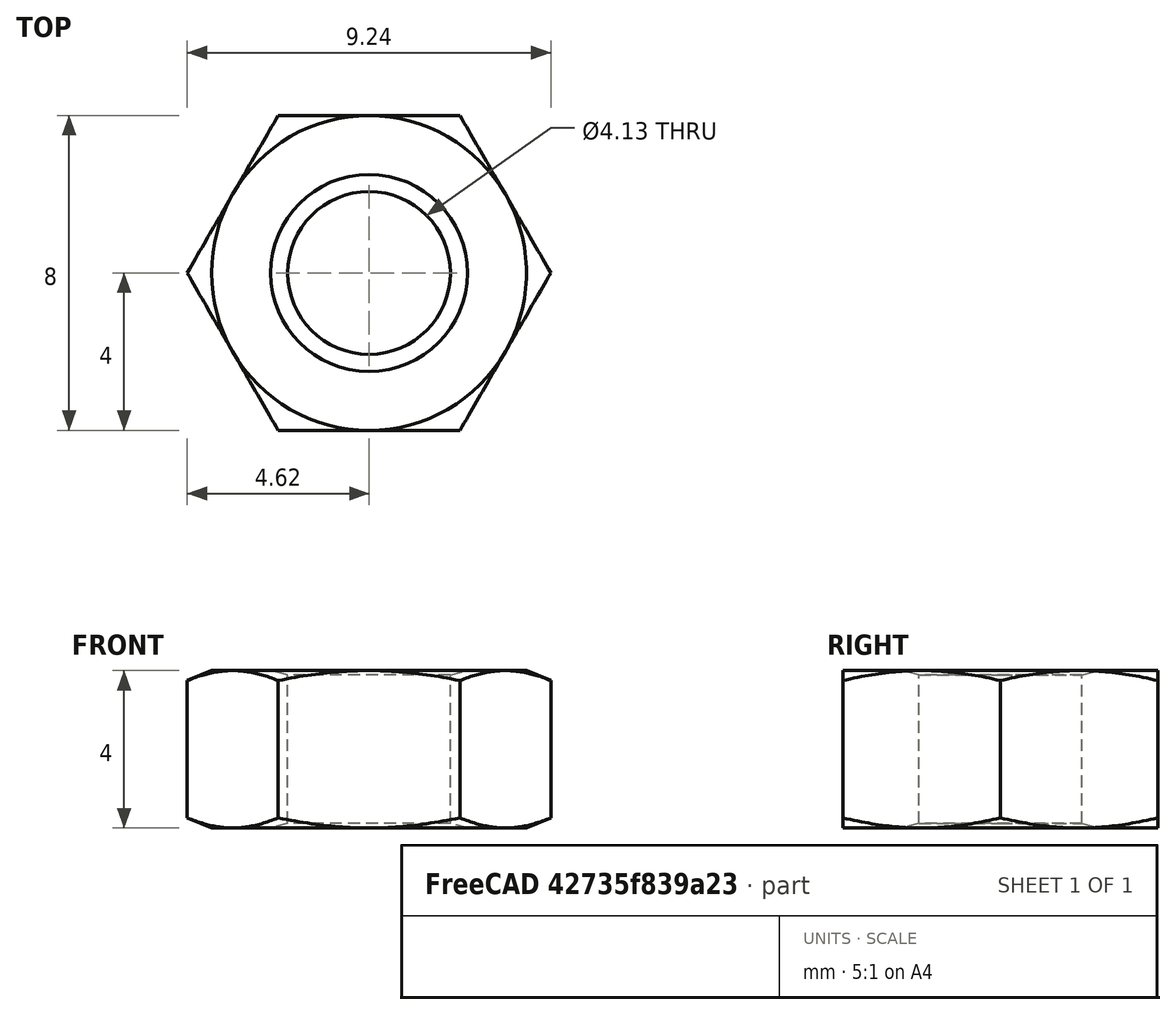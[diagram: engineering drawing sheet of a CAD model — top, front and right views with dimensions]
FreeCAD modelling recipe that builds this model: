
FCSTD DOCUMENT  (FreeCAD 1.0R39319 (Git))
Label: Assy_Foot
License: All rights reserved
LicenseURL: https://en.wikipedia.org/wiki/All_rights_reserved
objects: App::DocumentObjectGroup×3, PartDesign::CoordinateSystem×1, App::FeaturePython×1, App::Link×1, Part::FeaturePython×1, App::Part×1
note: 2 computed .brp shape members not serialized (recipe doc carries the construction recipe); baked Part::Feature solids carry a one-line shape summary decoded from their .brp
EXTERNAL_REF file=../../Part/Print/Foot.FCStd obj=base
EXTERNAL_REF file=../../Part/Print/Foot.FCStd obj=Part

FEATURE [App::DocumentObjectGroup] Parts
FEATURE [PartDesign::CoordinateSystem] LCS_Origin
  AttacherType = Attacher::AttachEngine3D
  AttachmentSupport = -> [X_Axis]
  MapMode = 2
FEATURE [App::DocumentObjectGroup] Constraints
FEATURE [App::FeaturePython] Variables  # WARN: FeaturePython — macro-defined, semantics opaque (R4)
  Type = App::PropertyContainer
FEATURE [App::DocumentObjectGroup] Configurations
FEATURE [App::Link] Foot
  AttachedBy = #base
  AttachedTo = Parent Assembly#LCS_Origin
  LinkPlacement = pos=(2e-15,0,0) rot=(0,0,1;1.5708rad)
  LinkedObject = -> <external ../../Part/Print/Foot.FCStd>#Part
  Placement = pos=(2e-15,0,0) rot=(0,0,1;1.5708rad)
  SolverId = Asm4EE
  expr: Placement = LCS_Origin.Placement * AttachmentOffset * Foot#base.Placement ^ -1
FEATURE [Part::FeaturePython] Nut  label="M5-Nut"  # WARN: FeaturePython — macro-defined, semantics opaque (R4)
  BaseObject = -> Foot [Body.Chamfer.Edge29]
  Diameter = 1
  Invert = false
  LeftHanded = false
  MatchOuter = false
  OffsetAngle = 0
  Placement = pos=(0,0,4) rot=(0,0,1;0rad)
  Thread = false
  Type = 33
FEATURE [App::Part] Assembly  label="Assy_Foot"
  AssemblyType = Part::Link
  Group = -> [LCS_Origin,Constraints,Variables,Configurations,Foot,Nut]
  Origin = -> Origin
  Type = Assembly

RESOLVED EXTERNAL PARTS (link-assembly join: the EXTERNAL_REF files above that resolve inside this repo's crawl, each included once):
---- part ../../Part/Print/Foot.FCStd = doc fcstd_07f4133909bb ----
FCSTD DOCUMENT  (FreeCAD 1.0R39319 (Git))
Label: Foot
License: All rights reserved
LicenseURL: https://en.wikipedia.org/wiki/All_rights_reserved
objects: Sketcher::SketchObject×3, PartDesign::Pocket×2, PartDesign::CoordinateSystem×2, PartDesign::Revolution×1, PartDesign::Fillet×1, PartDesign::Chamfer×1, PartDesign::Body×1, App::Part×1
note: 24 computed .brp shape members not serialized (recipe doc carries the construction recipe); baked Part::Feature solids carry a one-line shape summary decoded from their .brp

FEATURE [Sketcher::SketchObject] Sketch
  ArcFitTolerance = 1e-06
  AttachmentSupport = -> [XZ_Plane001]
  FullyConstrained = true
  MakeInternals = false
  MapMode = 5
  Placement = pos=(0,0,0) rot=(1,0,0;1.5708rad)
  sketch-geometry (6):
    g0: LineSegment StartX=0 StartY=0 StartZ=0 EndX=0 EndY=9 EndZ=0
    g1: LineSegment StartX=0 StartY=9 StartZ=0 EndX=5.5 EndY=9 EndZ=0
    g2: LineSegment StartX=5.5 StartY=9 StartZ=0 EndX=5.5 EndY=5 EndZ=0
    g3: LineSegment StartX=5.5 StartY=5 StartZ=0 EndX=7.5 EndY=5 EndZ=0
    g4: LineSegment StartX=7.5 StartY=5 StartZ=0 EndX=7.5 EndY=0 EndZ=0
    g5: LineSegment StartX=7.5 StartY=0 StartZ=0 EndX=0 EndY=0 EndZ=0
  constraints (17):
    c: Coincident(g-1,g0)
    c: PointOnObject(g0,g-2)
    c: Coincident(g0,g1)
    c: Horizontal(g1)
    c: Coincident(g1,g2)
    c: Vertical(g2)
    c: Coincident(g2,g3)
    c: Horizontal(g3)
    c: Coincident(g3,g4)
    c: PointOnObject(g4,g-1)
    c: Vertical(g4)
    c: Coincident(g4,g5)
    c: Coincident(g5,g0)
    c: Distance(g5,g3) = 5
    c: Distance(g3,g1) = 4
    c: Distance(g4,g0) = 7.5
    c: Distance(g0,g2) = 5.5
FEATURE [PartDesign::Revolution] Revolution
  Angle = 360
  Angle2 = 60
  Axis = (0,2e-16,1)
  Base = (0,0,0)
  Placement = pos=(0,0,0) rot=(1,0,0;1.5708rad)
  Profile = -> Sketch
  ReferenceAxis = -> Sketch [V_Axis]
  Refine = true
  Reversed = true
  Suppressed = false
  Type = 0
FEATURE [Sketcher::SketchObject] Sketch001
  ArcFitTolerance = 1e-06
  AttachmentSupport = -> [Revolution]
  FullyConstrained = true
  MakeInternals = false
  MapMode = 5
  Placement = pos=(0,4e-15,9) rot=(0,0,1;3.14159rad)
  sketch-geometry (1):
    g0: Circle CenterX=0 CenterY=0 CenterZ=0 NormalX=0 NormalY=0 NormalZ=1 AngleXU=0 Radius=3
  constraints (2):
    c: Coincident(g0,g-1)
    c: Diameter(g0) = 6
FEATURE [PartDesign::Pocket] Pocket
  BaseFeature = -> Revolution
  Direction = (0,0,-1)
  Length = 5
  Length2 = 5
  Placement = pos=(0,0,0) rot=(1,0,0;1.5708rad)
  Profile = -> Sketch001
  ReferenceAxis = -> Sketch001 [N_Axis]
  Refine = true
  Suppressed = false
  Type = 1
FEATURE [Sketcher::SketchObject] Sketch002
  ArcFitTolerance = 1e-06
  AttachmentSupport = -> [Pocket]
  FullyConstrained = true
  MakeInternals = false
  MapMode = 5
  Placement = pos=(0,4e-15,9) rot=(0,0,1;3.14159rad)
  sketch-geometry (7):
    g0: LineSegment StartX=4.11362 StartY=2.375 StartZ=0 EndX=0 EndY=4.75 EndZ=0
    g1: LineSegment StartX=0 StartY=4.75 StartZ=0 EndX=-4.11362 EndY=2.375 EndZ=0
    g2: LineSegment StartX=-4.11362 StartY=2.375 StartZ=0 EndX=-4.11362 EndY=-2.375 EndZ=0
    g3: LineSegment StartX=-4.11362 StartY=-2.375 StartZ=0 EndX=-1.8e-15 EndY=-4.75 EndZ=0
    g4: LineSegment StartX=-1.5e-15 StartY=-4.75 StartZ=0 EndX=4.11362 EndY=-2.375 EndZ=0
    g5: LineSegment StartX=4.11362 StartY=-2.375 StartZ=0 EndX=4.11362 EndY=2.375 EndZ=0
    g6: Circle [constr] CenterX=0 CenterY=0 CenterZ=0 NormalX=0 NormalY=0 NormalZ=1 AngleXU=0 Radius=4.75
  constraints (16):
    c: Coincident(g0,g1)
    c: Coincident(g1,g2)
    c: Coincident(g2,g3)
    c: Coincident(g3,g4)
    c: Coincident(g4,g5)
    c: Coincident(g5,g0)
    c: Equal(g0, g1-g5) x5
    c: PointOnObject(g0,g6)
    c: PointOnObject(g1,g6)
    c: PointOnObject(g2,g6)
    c: PointOnObject(g3,g6)
    c: PointOnObject(g4,g6)
    c: PointOnObject(g5,g6)
    c: Coincident(g6,g-1)
    c: Diameter(g6) = 9.5
    c: PointOnObject(g0,g-2)
FEATURE [PartDesign::Pocket] Pocket001
  BaseFeature = -> Pocket
  Direction = (0,0,-1)
  Length = 5
  Length2 = 5
  Placement = pos=(0,0,0) rot=(1,0,0;1.5708rad)
  Profile = -> Sketch002
  ReferenceAxis = -> Sketch002 [N_Axis]
  Refine = true
  Suppressed = false
  Type = 0
FEATURE [PartDesign::Fillet] Fillet
  Base = -> Pocket001 [Edge22]
  BaseFeature = -> Pocket001
  Placement = pos=(0,0,0) rot=(1,0,0;1.5708rad)
  Radius = 1
  Refine = true
  SupportTransform = false
  Suppressed = false
  UseAllEdges = false
FEATURE [PartDesign::Chamfer] Chamfer
  Angle = 45
  Base = -> Fillet [Edge5]
  BaseFeature = -> Fillet
  ChamferType = 0
  FlipDirection = false
  Placement = pos=(0,0,0) rot=(1,0,0;1.5708rad)
  Refine = true
  Size = 0.5
  Size2 = 1
  SupportTransform = false
  Suppressed = false
  UseAllEdges = false
FEATURE [PartDesign::Body] Body  label="Foot001"
  AllowCompound = false
  Group = -> [Sketch,Revolution,Sketch001,Pocket,Sketch002,Pocket001,Fillet,Chamfer]
  Origin = -> Origin001
  Tip = -> Chamfer
FEATURE [PartDesign::CoordinateSystem] nut
  AttacherType = Attacher::AttachEngine3D
  AttachmentSupport = -> [Chamfer]
  MapMode = 11
  Placement = pos=(0,2.9e-15,4) rot=(0,0,-1;1.5708rad)
FEATURE [PartDesign::CoordinateSystem] base
  AttacherType = Attacher::AttachEngine3D
  AttachmentSupport = -> [Chamfer]
  MapMode = 11
  Placement = pos=(0,2e-15,0) rot=(0,0,-1;1.5708rad)
FEATURE [App::Part] Part  label="Foot"
  Group = -> [Body,nut,base]
  Origin = -> Origin
